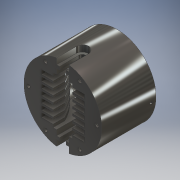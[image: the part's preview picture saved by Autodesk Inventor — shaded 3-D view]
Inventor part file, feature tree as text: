
AUTODESK INVENTOR PART (.ipt)
format: ipt  version: 2016 (Build 200138000, 138)  size: 501,760 bytes
history: native  units: mm
features: sketch x9, extrude x8, plane x4, projected_geometry x4, mirror x2, pattern_linear x2, loft x1, fillet x1, hole x1, pattern_circular x1, other x1
ambient origin geometry x8: Origin, YZ Plane, XZ Plane, XY Plane, X Axis, Y Axis, Z Axis, Center Point
bodies: Solid1 (feature_tree)
feature tree (34):
  sketch  "Sketch1"  dims[d0=100.0mm d1=70.0mm d2=0.0mm]
  extrude  "Extrusion1"  Depth=70.0mm TaperAngle=0.0deg
  extrude  "Extrusion2"  Depth=2.6mm
  sketch  "Sketch18"  dims[d3=35.0mm d4=50.0mm d5=50.0mm d6=0.0mm d7=0.0mm d71=2.6mm]
  plane  "Work Plane3"
  plane  "Work Plane4"
  extrude  "Extrusion11"  Depth=8.0mm
  loft  "Loft3"
  mirror  "Mirror1"
  extrude  "Extrusion12"  Depth=16.0mm
  extrude  "Extrusion13"  Depth=5.0mm
  pattern_linear  "Rectangular Pattern2"  Count1=5  [1 undecoded]
  extrude  "Extrusion14"  Depth=4.0mm TaperAngle=0.0deg
  pattern_linear  "Rectangular Pattern3"  Spacing1=0.0mm  [1 undecoded]
  fillet  "Fillet5"  [1 undecoded]
  hole  "Hole2"  [1 undecoded]
  pattern_circular  "Circular Pattern1"  [2 undecoded]
  extrude  "Extrusion15"  Depth=4.0mm
  plane  "Work Plane5"
  plane  "Work Plane6"
  extrude  "Extrusion16"  Depth=4.0mm TaperAngle=0.0deg
  mirror  "Mirror2"
  projected_geometry  "Projected Loop5"
  sketch  "Sketch22"  dims[d100=5.0mm d101=8.0mm]
  projected_geometry  "Projected Loop8"
  other  "Edges6"
  sketch  "Sketch23"  dims[d102=16.0mm d105=60.0deg]
  sketch  "Sketch24"  dims[d106=16.0mm d107=2.0mm]
  sketch  "Sketch25"  dims[d108=6.981317mm d109=5.0mm]
  sketch  "Sketch27"  dims[d110=35.0mm]
  sketch  "Sketch28"  dims[d111=15.0mm]
  projected_geometry  "Projected Loop9"
  sketch  "Sketch30"  dims[d112=5.0mm d117=50.0mm d118=70.0mm d119=20.0mm d120=0.0mm d121=0.0mm d122=90.0deg d123=0.0mm d124=90.0deg d125=20.0mm d126=0.0mm d127=5.5mm d128=55.0mm d129=20.0mm d130=0.0mm d131=26.5mm d132=70.0mm d134=8.0mm d136=45.0deg d137=6.0mm d138=1.6mm d139=0.0mm d140=30.0mm d142=10.0mm d143=10.0mm d144=6.0mm d145=4.2mm d146=6.0mm d147=4.0mm d148=2.0mm d149=90.0deg d150=8.0mm d151=20.594885mm d152=60.0mm d153=360.0deg d155=3.2mm d156=1600.0mm d157=0.0mm d158=4.2mm d159=4.0mm d160=0.0mm d161=7.0mm]
  projected_geometry  "Project Cut Edges3"
note: 6 required parameter values undecoded (feature->parameter linkage not recoverable at this tier; creation-order binding heuristic only, values carry confidence <= 0.55)
